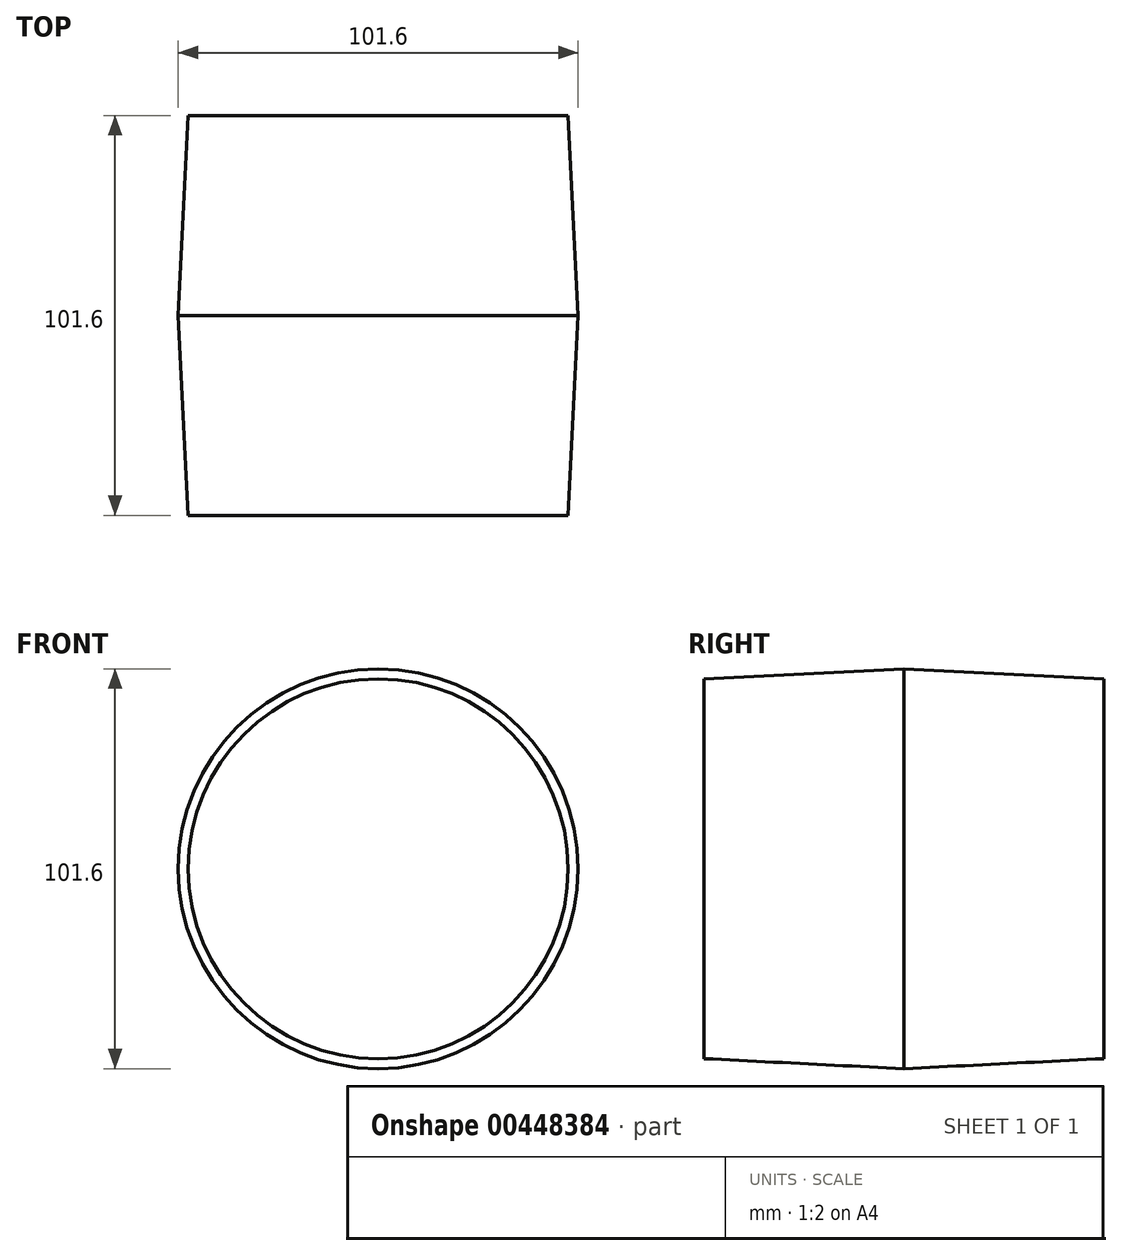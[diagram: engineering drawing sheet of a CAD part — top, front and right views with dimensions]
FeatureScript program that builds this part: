
annotation { "Feature Type Name" : "Feature", "Feature Type Description" : "" }
export const myFeature = defineFeature(function(context is Context, id is Id, definition is map)
    precondition{}
    {
        {
            var Q0;
            Q0=qCreatedBy(makeId("Front.planeOp"),FACE);
            var sketch = newSketch(context, id + "F0", { "sketchPlane" : qUnion([Q0])});
            skCircle(sketch, "E0", {"center": v(0, 0) * mm, "radius": 50.8 * mm});
            skSolve(sketch);
        }
        {
            var Q0;
            Q0 = qSketchRegion(id + "F0", true);
            extrude(context, id + "F1", {"entities" : qUnion([Q0]), "depth" : 101.6 * mm});
        }
        {
            var Q0;
            Q0=makeQuery(id+"F1.opExtrude","SWEPT_FACE",FACE,{"disambiguationData":[OSD([sQuery(id+"F0.wireOp",EDGE,"E0")])]});
            chamfer(context, id + "F2", {"entities" : qUnion([Q0]), "chamferType" : ChamferType.TWO_OFFSETS, "width1" : 50.8 * mm, "oppositeDirection" : false, "width2" : 2.54 * mm, "tangentPropagation" : true});
        }
    });
